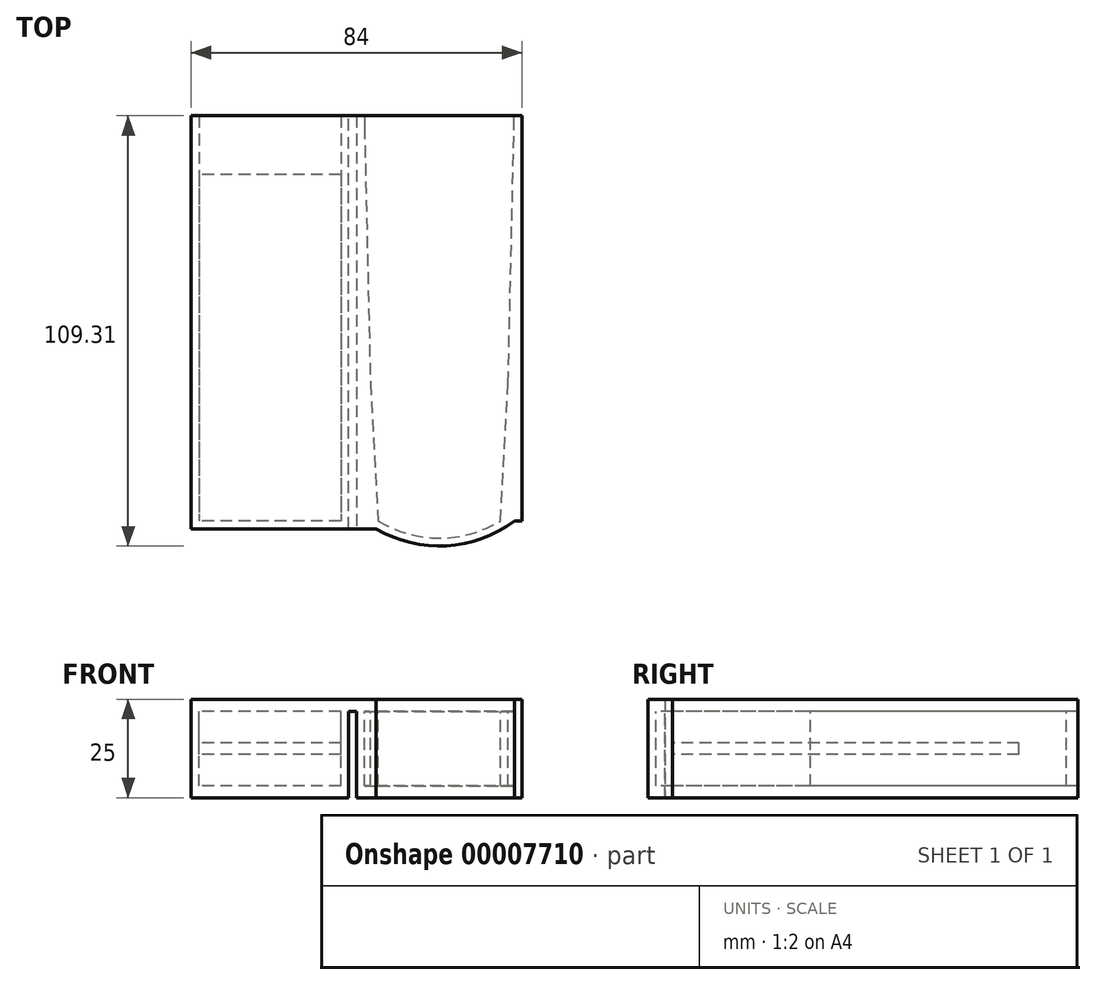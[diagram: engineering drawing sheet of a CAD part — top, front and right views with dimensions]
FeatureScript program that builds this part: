
annotation { "Feature Type Name" : "Feature", "Feature Type Description" : "" }
export const myFeature = defineFeature(function(context is Context, id is Id, definition is map)
    precondition{}
    {
        {
            var Q0;
            Q0=qCreatedBy(makeId("Top.planeOp"),FACE);
            var sketch = newSketch(context, id + "F0", { "sketchPlane" : qUnion([Q0])});
            skLineSegment(sketch, "E0", {"start": v(0, 51.5) * mm, "end": v(0, -51.5) * mm, "construction": true});
            skLineSegment(sketch, "E1", {"start": v(-15.5, -51.5) * mm, "end": v(15.5, -51.5) * mm, "construction": true});
            skLineSegment(sketch, "E2", {"start": v(15.5, -51.5) * mm, "end": v(17.5, -16.5) * mm});
            skLineSegment(sketch, "E3", {"start": v(17.5, -16.5) * mm, "end": v(-17.5, -16.5) * mm, "construction": true});
            skLineSegment(sketch, "E4.0", {"start": v(19, 48.5) * mm, "end": v(-19, 48.5) * mm, "construction": true});
            skPoint(sketch, "E5", {"position": v(0, 48.5) * mm});
            skPoint(sketch, "E6", {"position": v(0, -16.5) * mm});
            skArc(sketch, "E7", {"start": v(-15.5, -51.5) * mm, "mid": v(0, -55.81) * mm, "end": v(15.5, -51.5) * mm});
            skLineSegment(sketch, "E8", {"start": v(17.5, -16.5) * mm, "end": v(19, 48.5) * mm});
            skLineSegment(sketch, "E9", {"start": v(19, 48.5) * mm, "end": v(19, 51.5) * mm});
            skLineSegment(sketch, "E10", {"start": v(19, 51.5) * mm, "end": v(-19, 51.5) * mm});
            skLineSegment(sketch, "E11", {"start": v(-19, 51.5) * mm, "end": v(-19, 48.5) * mm});
            skLineSegment(sketch, "E12", {"start": v(-19, 48.5) * mm, "end": v(-17.5, -16.5) * mm});
            skLineSegment(sketch, "E13", {"start": v(-17.5, -16.5) * mm, "end": v(-15.5, -51.5) * mm});
            skLineSegment(sketch, "E14.0", {"start": v(-25, 51.5) * mm, "end": v(-25, -51.5) * mm});
            skLineSegment(sketch, "E15.0", {"start": v(21, -51.5) * mm, "end": v(21, 51.5) * mm});
            skLineSegment(sketch, "E16", {"start": v(-19, 51.5) * mm, "end": v(-25, 51.5) * mm});
            skLineSegment(sketch, "E17", {"start": v(19, 51.5) * mm, "end": v(21, 51.5) * mm});
            skLineSegment(sketch, "E18", {"start": v(-25, -51.5) * mm, "end": v(21, -51.5) * mm});
            skArc(sketch, "E19.0", {"start": v(-16.05, -53.5) * mm, "mid": v(1.82, -57.76) * mm, "end": v(19.09, -51.5) * mm});
            skLineSegment(sketch, "E20.0", {"start": v(-61, 51.5) * mm, "end": v(-61, -51.5) * mm});
            skLineSegment(sketch, "E21.0", {"start": v(-63, 51.5) * mm, "end": v(-63, -51.5) * mm});
            skLineSegment(sketch, "E22", {"start": v(-25, -51.5) * mm, "end": v(-63, -51.5) * mm});
            skLineSegment(sketch, "E23", {"start": v(-25, 51.5) * mm, "end": v(-63, 51.5) * mm});
            skLineSegment(sketch, "E24.0", {"start": v(-16.05, -53.5) * mm, "end": v(-63, -53.5) * mm});
            skLineSegment(sketch, "E25", {"start": v(-63, -51.5) * mm, "end": v(-63, -53.5) * mm});
            skLineSegment(sketch, "E26", {"start": v(-21, 51.5) * mm, "end": v(-21, -53.5) * mm});
            skLineSegment(sketch, "E27", {"start": v(-23, -53.5) * mm, "end": v(-23, 51.5) * mm});
            skSolve(sketch);
        }
        {
            var Q0;
            {var subQ0=sQuery(id+"F0.wireOp",EDGE,"E20.0");Q0=makeQuery(id+"F0.imprint","IMPRINT",FACE,{"disambiguationData":[TD([[makeQuery(id+"F0.imprint","IMPRINT",EDGE,{"derivedFrom":subQ0}),-1.0]])]});}
            var Q1;
            {var subQ0=sQuery(id+"F0.wireOp",EDGE,"E14.0");Q1=makeQuery(id+"F0.imprint","IMPRINT",FACE,{"disambiguationData":[TD([[makeQuery(id+"F0.imprint","IMPRINT",EDGE,{"derivedFrom":subQ0}),-1.0]])]});}
            var Q2;
            Q2=makeQuery(id+"F0.imprint","IMPRINT",FACE,{"disambiguationData":[TD([[makeQuery(id+"F0.imprint","IMPRINT",EDGE,{"derivedFrom":sQuery(id+"F0.wireOp",EDGE,"E11")}),-1.0]])]});
            var Q3;
            {var subQ2=sQuery(id+"F0.wireOp",EDGE,"E2");Q3=makeQuery(id+"F0.imprint","IMPRINT",FACE,{"disambiguationData":[TD([[makeQuery(id+"F0.imprint","IMPRINT",EDGE,{"derivedFrom":subQ2}),1.0]])]});}
            var Q4;
            {var subQ1=sQuery(id+"F0.wireOp",EDGE,"E2");Q4=makeQuery(id+"F0.imprint","IMPRINT",FACE,{"disambiguationData":[TD([[makeQuery(id+"F0.imprint","IMPRINT",EDGE,{"derivedFrom":subQ1}),-1.0]])]});}
            var Q5;
            {var subQ0=sQuery(id+"F0.wireOp",EDGE,"E7");Q5=makeQuery(id+"F0.imprint","IMPRINT",FACE,{"disambiguationData":[TD([[makeQuery(id+"F0.imprint","IMPRINT",EDGE,{"derivedFrom":subQ0}),1.0]])]});}
            var Q6;
            {var subQ0=sQuery(id+"F0.wireOp",EDGE,"E7");Q6=makeQuery(id+"F0.imprint","IMPRINT",FACE,{"disambiguationData":[TD([[makeQuery(id+"F0.imprint","IMPRINT",EDGE,{"derivedFrom":subQ0}),-1.0]])]});}
            var Q7;
            {var subQ0=sQuery(id+"F0.wireOp",EDGE,"E26");var subQ1=sQuery(id+"F0.wireOp",EDGE,"E16");var subQ2=makeQuery(id+"F0.imprint","INTERSECT",VERTEX,{"derivedFrom":[subQ1,subQ0]});Q7=makeQuery(id+"F0.imprint","IMPRINT",FACE,{"disambiguationData":[TD([[makeQuery(id+"F0.imprint","IMPRINT",EDGE,{"disambiguationData":[TD([[subQ2,-1.0]])],"derivedFrom":subQ1}),1.0]])]});}
            var Q8;
            {var subQ0=sQuery(id+"F0.wireOp",EDGE,"E14.0");Q8=makeQuery(id+"F0.imprint","IMPRINT",FACE,{"disambiguationData":[TD([[makeQuery(id+"F0.imprint","IMPRINT",EDGE,{"derivedFrom":subQ0}),1.0]])]});}
            var Q9;
            {var subQ0=sQuery(id+"F0.wireOp",EDGE,"E27");var subQ1=sQuery(id+"F0.wireOp",EDGE,"E18");var subQ2=makeQuery(id+"F0.imprint","INTERSECT",VERTEX,{"derivedFrom":[subQ1,subQ0]});Q9=makeQuery(id+"F0.imprint","IMPRINT",FACE,{"disambiguationData":[TD([[makeQuery(id+"F0.imprint","IMPRINT",EDGE,{"disambiguationData":[TD([[subQ2,-1.0]])],"derivedFrom":subQ1}),-1.0]])]});}
            var Q10;
            {var subQ4=sQuery(id+"F0.wireOp",EDGE,"E25");Q10=makeQuery(id+"F0.imprint","IMPRINT",FACE,{"disambiguationData":[TD([[makeQuery(id+"F0.imprint","IMPRINT",EDGE,{"derivedFrom":subQ4}),1.0]])]});}
            extrude(context, id + "F1", {"entities" : qUnion([Q0, Q1, Q2, Q3, Q4, Q5, Q6, Q7, Q8, Q9, Q10]), "depth" : 3 * mm, "offsetDistance" : 25 * mm});
        }
        {
            var Q0;
            {var subQ1=sQuery(id+"F0.wireOp",EDGE,"E2");Q0=makeQuery(id+"F0.imprint","IMPRINT",FACE,{"disambiguationData":[TD([[makeQuery(id+"F0.imprint","IMPRINT",EDGE,{"derivedFrom":subQ1}),-1.0]])]});}
            var Q1;
            Q1=makeQuery(id+"F0.imprint","IMPRINT",FACE,{"disambiguationData":[TD([[makeQuery(id+"F0.imprint","IMPRINT",EDGE,{"derivedFrom":sQuery(id+"F0.wireOp",EDGE,"E11")}),-1.0]])]});
            var Q2;
            {var subQ0=sQuery(id+"F0.wireOp",EDGE,"E7");Q2=makeQuery(id+"F0.imprint","IMPRINT",FACE,{"disambiguationData":[TD([[makeQuery(id+"F0.imprint","IMPRINT",EDGE,{"derivedFrom":subQ0}),-1.0]])]});}
            var Q3;
            {var subQ0=sQuery(id+"F0.wireOp",EDGE,"E20.0");Q3=makeQuery(id+"F0.imprint","IMPRINT",FACE,{"disambiguationData":[TD([[makeQuery(id+"F0.imprint","IMPRINT",EDGE,{"derivedFrom":subQ0}),-1.0]])]});}
            var Q4;
            {var subQ0=sQuery(id+"F0.wireOp",EDGE,"E14.0");Q4=makeQuery(id+"F0.imprint","IMPRINT",FACE,{"disambiguationData":[TD([[makeQuery(id+"F0.imprint","IMPRINT",EDGE,{"derivedFrom":subQ0}),1.0]])]});}
            var Q5;
            {var subQ4=sQuery(id+"F0.wireOp",EDGE,"E25");Q5=makeQuery(id+"F0.imprint","IMPRINT",FACE,{"disambiguationData":[TD([[makeQuery(id+"F0.imprint","IMPRINT",EDGE,{"derivedFrom":subQ4}),1.0]])]});}
            extrude(context, id + "F2", {"entities" : qUnion([Q0, Q1, Q2, Q3, Q4, Q5]), "operationType" : NewBodyOperationType.ADD, "oppositeDirection" : true, "depth" : 22 * mm, "offsetDistance" : 25 * mm});
        }
        {
            var Q0;
            {var subQ0=sQuery(id+"F0.wireOp",EDGE,"E16");var subQ2=sQuery(id+"F0.wireOp",EDGE,"E10");var subQ3=sQuery(id+"F0.wireOp",EDGE,"E23");var subQ4=sQuery(id+"F0.wireOp",EDGE,"E17");Q0=makeQuery(id+"F2.boolean.opBoolean","SPLIT",FACE,{"disambiguationData":[TD([makeQuery(id+"F2.opExtrude","SWEPT_FACE",FACE,{"disambiguationData":[OSD([sQuery(id+"F0.wireOp",EDGE,"E2")])]})])],"derivedFrom":makeQuery(id+"F1.opExtrude","CAP_FACE",FACE,{"disambiguationData":[OSD([subQ2,sQuery(id+"F0.wireOp",EDGE,"E15.0"),subQ0,subQ4,sQuery(id+"F0.wireOp",EDGE,"E18"),sQuery(id+"F0.wireOp",EDGE,"E19.0"),sQuery(id+"F0.wireOp",EDGE,"E21.0"),subQ3,sQuery(id+"F0.wireOp",EDGE,"E24.0"),sQuery(id+"F0.wireOp",EDGE,"E25")])],"isStart":true})});}
            var Q1;
            {var subQ0=sQuery(id+"F0.wireOp",EDGE,"E16");var subQ1=sQuery(id+"F0.wireOp",EDGE,"E10");var subQ2=sQuery(id+"F0.wireOp",EDGE,"E23");var subQ3=sQuery(id+"F0.wireOp",EDGE,"E14.0");var subQ4=sQuery(id+"F0.wireOp",EDGE,"E17");Q1=makeQuery(id+"F2.boolean.opBoolean","SPLIT",FACE,{"disambiguationData":[TD([makeQuery(id+"F2.opExtrude","SWEPT_FACE",FACE,{"disambiguationData":[OSD([subQ3])]})])],"derivedFrom":makeQuery(id+"F1.opExtrude","CAP_FACE",FACE,{"disambiguationData":[OSD([subQ1,sQuery(id+"F0.wireOp",EDGE,"E15.0"),subQ0,subQ4,sQuery(id+"F0.wireOp",EDGE,"E18"),sQuery(id+"F0.wireOp",EDGE,"E19.0"),sQuery(id+"F0.wireOp",EDGE,"E21.0"),subQ2,sQuery(id+"F0.wireOp",EDGE,"E24.0"),sQuery(id+"F0.wireOp",EDGE,"E25")])],"isStart":true})});}
            extrude(context, id + "F3", {"entities" : qUnion([Q0, Q1]), "operationType" : NewBodyOperationType.ADD, "depth" : 22 * mm, "offsetDistance" : 25 * mm, "hasSecondDirection" : true, "secondDirectionOppositeDirection" : false, "secondDirectionDepth" : 19 * mm});
        }
        {
            var Q0;
            {var subQ0=sQuery(id+"F0.wireOp",EDGE,"E14.0");Q0=makeQuery(id+"F0.imprint","IMPRINT",FACE,{"disambiguationData":[TD([[makeQuery(id+"F0.imprint","IMPRINT",EDGE,{"derivedFrom":subQ0}),-1.0]])]});}
            extrude(context, id + "F4", {"entities" : qUnion([Q0]), "operationType" : NewBodyOperationType.ADD, "oppositeDirection" : true, "depth" : 11 * mm, "offsetDistance" : 25 * mm, "hasSecondDirection" : true, "secondDirectionOppositeDirection" : true, "secondDirectionDepth" : 8 * mm});
        }
        {
            var Q0;
            {var subQ0=sQuery(id+"F0.wireOp",EDGE,"E23");var subQ1=sQuery(id+"F0.wireOp",EDGE,"E17");var subQ2=sQuery(id+"F0.wireOp",EDGE,"E16");var subQ3=sQuery(id+"F0.wireOp",EDGE,"E10");Q0=makeQuery(id+"F4.boolean.opBoolean","MERGE",FACE,{"derivedFrom":[makeQuery(id+"F3.boolean.opBoolean","MERGE",FACE,{"derivedFrom":[makeQuery(id+"F2.boolean.opBoolean","MERGE",FACE,{"derivedFrom":[makeQuery(id+"F1.opExtrude","SWEPT_FACE",FACE,{"disambiguationData":[OSD([subQ3,subQ2,subQ1,subQ0])]}),makeQuery(id+"F2.opExtrude","SWEPT_FACE",FACE,{"disambiguationData":[OSD([subQ2])]}),makeQuery(id+"F2.opExtrude","SWEPT_FACE",FACE,{"disambiguationData":[OSD([subQ1])]}),makeQuery(id+"F2.opExtrude","SWEPT_FACE",FACE,{"disambiguationData":[OSD([subQ0])]})]}),makeQuery(id+"F3.opExtrude","SWEPT_FACE",FACE,{"disambiguationData":[OSD([subQ3,subQ2,subQ1,subQ0])]})]}),makeQuery(id+"F4.opExtrude","SWEPT_FACE",FACE,{"disambiguationData":[OSD([subQ0])]})]});}
            var sketch = newSketch(context, id + "F5", { "sketchPlane" : qUnion([Q0])});
            skLineSegment(sketch, "E28", {"start": v(25, -11) * mm, "end": v(25, -8) * mm});
            skLineSegment(sketch, "E29", {"start": v(61, -11) * mm, "end": v(61, -8) * mm});
            skSolve(sketch);
        }
        {
            var Q0;
            Q0=makeQuery(id+"F5.imprint","IMPRINT",FACE,{"disambiguationData":[TD([[makeQuery(id+"F5.imprint","IMPRINT",EDGE,{"derivedFrom":sQuery(id+"F5.wireOp",EDGE,"E28")}),-1.0]])]});
            extrude(context, id + "F6", {"entities" : qUnion([Q0]), "operationType" : NewBodyOperationType.REMOVE, "oppositeDirection" : true, "depth" : 15 * mm, "offsetDistance" : 25 * mm});
        }
    });
